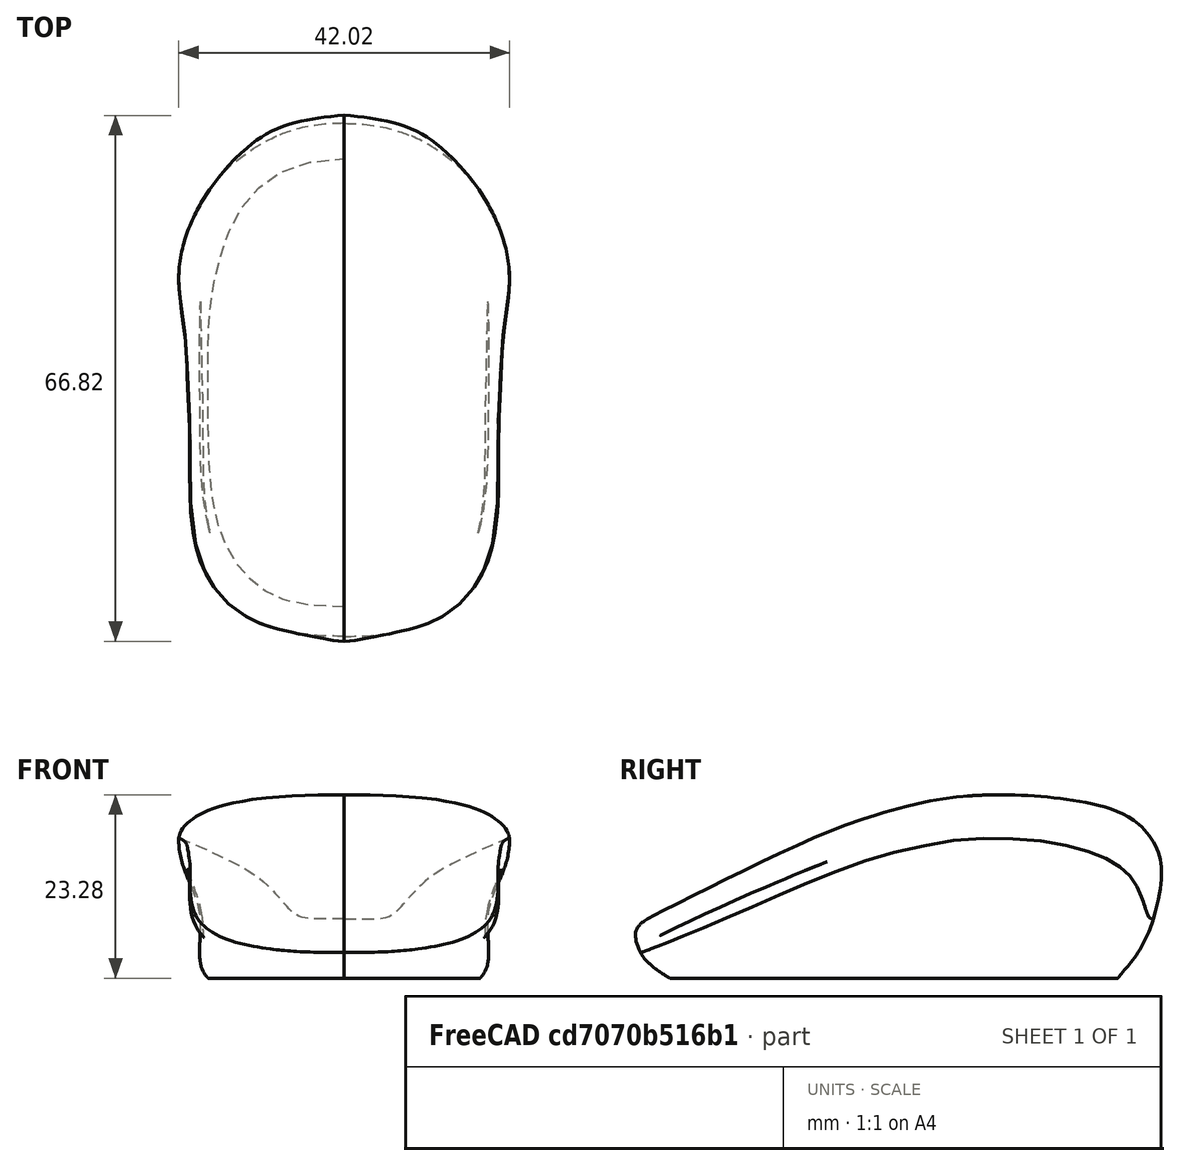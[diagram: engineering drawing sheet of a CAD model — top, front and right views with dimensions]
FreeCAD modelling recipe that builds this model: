
FCSTD DOCUMENT  (FreeCAD 1.0R38643 (Git))
Label: mouse
License: All rights reserved
LicenseURL: http://en.wikipedia.org/wiki/All_rights_reserved
objects: Part::FeaturePython×15, Sketcher::SketchObject×8, Image::ImagePlane×2, Part::Feature×2, Part::Mirroring×1, Part::RuledSurface×1, PartDesign::FeatureBase×1, PartDesign::Body×1, App::DocumentObjectGroup×1
note: 38 computed .brp shape members not serialized (recipe doc carries the construction recipe); baked Part::Feature solids carry a one-line shape summary decoded from their .brp

FEATURE [Image::ImagePlane] ai_mouse_top  label="ai-mouse-top"
  Placement = pos=(0,0,0) rot=(0,0,1;3.14159rad)
  XSize = 43.9769
  YSize = 68
  expr: XSize = 49.28 / 76.2 * YSize
FEATURE [Image::ImagePlane] ai_mouse_side  label="ai-mouse-side"
  Placement = pos=(-2.6e-15,0,11.5) rot=(-0.707107,0,-0.707107;3.14159rad)
  XSize = 31.4299
  YSize = 68
  expr: XSize = 35.22 / 76.2 * YSize
FEATURE [Sketcher::SketchObject] Sketch
  ArcFitTolerance = 0
  FullyConstrained = false
  MakeInternals = false
  sketch-geometry (33):
    g0-g16: Circle [constr] x17 (B-spline internal-alignment scaffolding for g17; pole/knot coordinates omitted)
    g17: BSplineCurve PolesCount=17 KnotsCount=15 Degree=3 IsPeriodic=0
    g18-g32: GeomPoint [constr] x15 (B-spline internal-alignment scaffolding for g17; pole/knot coordinates omitted)
  constraints (9):
    c: Weight(g0) = 1
    c: Equal(g0, g1-g16) x16
    c: InternalAlignment(g0-g16 -> g17) x17
    c: InternalAlignment(g18-g32 -> g17) x15
    c: PointOnObject(g0,g-2)
    c: PointOnObject(g7,g-1)
    c: PointOnObject(g16,g-2)
    c: Horizontal(g1,g17)
    c: Horizontal(g17,g15)
FEATURE [Sketcher::SketchObject] Sketch001
  ArcFitTolerance = 0
  ExternalGeometry = -> [Sketch]
  FullyConstrained = false
  MakeInternals = false
  Placement = pos=(0,0,0) rot=(0.57735,0.57735,0.57735;2.0944rad)
  sketch-geometry (29):
    g0: LineSegment [constr] StartX=-32.3494 StartY=0 StartZ=0 EndX=-32.3494 EndY=16.7331 EndZ=0
    g1: LineSegment [constr] StartX=32.8081 StartY=0 StartZ=0 EndX=32.8081 EndY=17.4154 EndZ=0
    g2-g15: Circle [constr] x14 (B-spline internal-alignment scaffolding for g16; pole/knot coordinates omitted)
    g16: BSplineCurve PolesCount=14 KnotsCount=12 Degree=3 IsPeriodic=0
    g17-g28: GeomPoint [constr] x12 (B-spline internal-alignment scaffolding for g16; pole/knot coordinates omitted)
  constraints (12):
    c: Coincident(g0,g-3)
    c: Vertical(g0)
    c: Coincident(g1,g-3)
    c: Vertical(g1)
    c: Weight(g2) = 1
    c: Equal(g2, g3-g15) x13
    c: InternalAlignment(g2-g15 -> g16) x14
    c: InternalAlignment(g17-g28 -> g16) x12
    c: PointOnObject(g3,g0)
    c: PointOnObject(g27,g1)
    c: Horizontal(g13,g27)
    c: Horizontal(g12,g13)
FEATURE [Part::FeaturePython] Mixed_curve  # WARN: FeaturePython — macro-defined, semantics opaque (R4)
  Active = false
  ApproxTolerance = 0.001
  Continuity = 5
  DegreeMax = 5
  DegreeMin = 3
  Direction1 = (0,0,0)
  Direction2 = (0,0,0)
  FillFace1 = false
  FillFace2 = false
  Parametrization = 0
  Samples = 100
  Shape1 = -> Sketch
  Shape2 = -> Sketch001
FEATURE [Sketcher::SketchObject] Sketch002
  ArcFitTolerance = 0
  ExternalGeometry = -> [Mixed_curve]
  FullyConstrained = false
  MakeInternals = false
  Placement = pos=(0,0,0) rot=(0.57735,0.57735,0.57735;2.0944rad)
  sketch-geometry (45):
    g0-g3: Circle [constr] x4 (B-spline internal-alignment scaffolding for g4; pole/knot coordinates omitted)
    g4: BSplineCurve PolesCount=4 KnotsCount=2 Degree=3 IsPeriodic=0
    g5: GeomPoint [constr] X=-28.6373 Y=0 Z=0
    g6: GeomPoint [constr] X=-32.3494 Y=3.25098 Z=0
    g7-g19: Circle [constr] x13 (B-spline internal-alignment scaffolding for g20; pole/knot coordinates omitted)
    g20: BSplineCurve PolesCount=13 KnotsCount=11 Degree=3 IsPeriodic=0
    g21-g31: GeomPoint [constr] x11 (B-spline internal-alignment scaffolding for g20; pole/knot coordinates omitted)
    g32-g36: Circle [constr] x5 (B-spline internal-alignment scaffolding for g37; pole/knot coordinates omitted)
    g37: BSplineCurve PolesCount=5 KnotsCount=3 Degree=3 IsPeriodic=0
    g38: GeomPoint [constr] X=32.8081 Y=7.53838 Z=0
    g39: GeomPoint [constr] X=30.7658 Y=3.14141 Z=0
    g40: GeomPoint [constr] X=28.2983 Y=0 Z=0
    g41: LineSegment [constr] StartX=-32.3494 StartY=3.25098 StartZ=0 EndX=-33.3149 EndY=5.18964 EndZ=0
    g42: LineSegment [constr] StartX=-32.3494 StartY=3.25098 StartZ=0 EndX=-31.6888 EndY=1.92452 EndZ=0
    g43: LineSegment [constr] StartX=32.8081 StartY=7.53838 StartZ=0 EndX=33.3398 EndY=9.66521 EndZ=0
    g44: LineSegment [constr] StartX=32.8081 StartY=7.53838 StartZ=0 EndX=32.5169 EndY=6.37396 EndZ=0
  constraints (33):
    c: Weight(g0) = 1
    c: Equal(g0,g1)
    c: Equal(g0,g2)
    c: Equal(g0,g3)
    c: InternalAlignment(g0-g3 -> g4) x4
    c: InternalAlignment(g5,g4)
    c: InternalAlignment(g6,g4)
    c: PointOnObject(g0,g-1)
    c: Coincident(g3,g-3)
    c: Weight(g7) = 1
    c: Equal(g7, g8-g19) x12
    c: InternalAlignment(g7-g19 -> g20) x13
    c: InternalAlignment(g21-g31 -> g20) x11
    c: Coincident(g7,g4)
    c: Coincident(g19,g-3)
    c: Weight(g32) = 1
    c: Equal(g32, g33-g36) x4
    c: InternalAlignment(g32-g36 -> g37) x5
    c: InternalAlignment(g38,g37)
    c: InternalAlignment(g39,g37)
    c: InternalAlignment(g40,g37)
    c: Coincident(g32,g20)
    c: PointOnObject(g36,g-1)
    c: Coincident(g41,g20)
    c: Coincident(g41,g8)
    c: Coincident(g42,g3)
    c: Coincident(g42,g2)
    c: Parallel(g41,g42)
    c: Coincident(g43,g37)
    c: Coincident(g43,g18)
    c: Coincident(g44,g19)
    c: Coincident(g44,g33)
    c: Parallel(g43,g44)
FEATURE [Sketcher::SketchObject] Sketch003
  ArcFitTolerance = 0
  ExternalGeometry = -> [Sketch002]
  FullyConstrained = false
  MakeInternals = false
  sketch-geometry (15):
    g0-g7: Circle [constr] x8 (B-spline internal-alignment scaffolding for g8; pole/knot coordinates omitted)
    g8: BSplineCurve PolesCount=8 KnotsCount=6 Degree=3 IsPeriodic=0
    g9-g14: GeomPoint [constr] x6 (B-spline internal-alignment scaffolding for g8; pole/knot coordinates omitted)
  constraints (9):
    c: Weight(g0) = 1
    c: Equal(g0, g1-g7) x7
    c: InternalAlignment(g0-g7 -> g8) x8
    c: InternalAlignment(g9-g14 -> g8) x6
    c: Coincident(g0,g-3)
    c: PointOnObject(g3,g-1)
    c: Coincident(g7,g-4)
    c: Horizontal(g8,g1)
    c: Horizontal(g8,g6)
FEATURE [Part::FeaturePython] Freehand_BSpline  # WARN: FeaturePython — macro-defined, semantics opaque (R4)
  Data = (5) [(20.9782,12.1976,17.7693),(20.7313,12.1868,15.241),(18.3975,12.1913,8.67744),(17.7344,12.1956,2.33636),(16.5708,12.2001,0)]
  DataType = [1,0,0,0,1]
  Parametrization = 1
  Periodic = false
  Support = -> [Mixed_curve,Sketch003]
  Tangents = (5) [(0,0,0),(0,0,0),(0,0,0),(0,0,0),(0,0,0)]
  Tolerance = 1e-07
FEATURE [Part::FeaturePython] JoinCurve  # WARN: FeaturePython — macro-defined, semantics opaque (R4)
  Active = false
  ApproxTolerance = 0.001
  Continuity = 5
  CornerBreak = false
  DegreeMax = 5
  DegreeMin = 3
  Edges = -> [Sketch002]
  ForceClosed = false
  ForceContact = true
  Parametrization = 0
  Reverse = false
  Samples = 100
  StartOffset = 0
  Tolerance = 0.01
FEATURE [Part::FeaturePython] JoinCurve001  # WARN: FeaturePython — macro-defined, semantics opaque (R4)
  Active = false
  ApproxTolerance = 0.001
  Continuity = 5
  CornerBreak = false
  DegreeMax = 5
  DegreeMin = 3
  Edges = -> [Sketch002]
  ForceClosed = false
  ForceContact = true
  Parametrization = 0
  Reverse = false
  Samples = 100
  StartOffset = 0
  Tolerance = 0.01
FEATURE [Part::FeaturePython] JoinCurve002  # WARN: FeaturePython — macro-defined, semantics opaque (R4)
  Active = false
  ApproxTolerance = 0.001
  Continuity = 5
  CornerBreak = false
  DegreeMax = 5
  DegreeMin = 3
  Edges = -> [Sketch003]
  ForceClosed = false
  ForceContact = true
  Parametrization = 0
  Reverse = false
  Samples = 100
  StartOffset = 0
  Tolerance = 0.01
FEATURE [Part::FeaturePython] Gordon  # WARN: FeaturePython — macro-defined, semantics opaque (R4)
  FlipNormal = false
  MaxCtrlPts = 80
  Output = 0
  SamplesU = 16
  SamplesV = 16
  Sources = -> [Mixed_curve,JoinCurve002,JoinCurve,Freehand_BSpline,JoinCurve001]
  Tol2D = 1e-05
  Tol3D = 0.01
FEATURE [Part::FeaturePython] Freehand_BSpline001  # WARN: FeaturePython — macro-defined, semantics opaque (R4)
  Data = (2) [(13.658,-28.9898,4.51691),(0,-31.4534,7.51518)]
  DataType = [1,1]
  Parametrization = 1
  Periodic = false
  Support = -> [Mixed_curve,Sketch002]
  Tangents = (2) [(0,0,0),(0,0,0)]
  Tolerance = 1e-07
FEATURE [Part::FeaturePython] Freehand_BSpline002  # WARN: FeaturePython — macro-defined, semantics opaque (R4)
  Data = (2) [(21.0023,12.8859,17.7665),(0,12.7657,23.283)]
  DataType = [1,1]
  Parametrization = 1
  Periodic = false
  Support = -> [Mixed_curve,Sketch002]
  Tangents = (2) [(0,0,0),(0,0,0)]
  Tolerance = 1e-07
FEATURE [Part::FeaturePython] Freehand_BSpline003  # WARN: FeaturePython — macro-defined, semantics opaque (R4)
  Data = (2) [(13.7278,28.0021,14.4972),(0,30.9529,19.5086)]
  DataType = [1,1]
  Parametrization = 1
  Periodic = false
  Support = -> [Mixed_curve,Sketch002]
  Tangents = (2) [(0,0,0),(0,0,0)]
  Tolerance = 1e-07
FEATURE [Sketcher::SketchObject] Sketch004
  ArcFitTolerance = 0
  ExternalGeometry = -> [Freehand_BSpline001,Freehand_BSpline002,Freehand_BSpline003]
  FullyConstrained = true
  MakeInternals = false
  Placement = pos=(0,0,0) rot=(0.57735,0.57735,0.57735;2.0944rad)
  sketch-geometry (3):
    g0: LineSegment StartX=-31.4534 StartY=7.51518 StartZ=0 EndX=-28.9898 EndY=4.51691 EndZ=0
    g1: LineSegment StartX=12.7657 StartY=23.283 StartZ=0 EndX=12.8859 EndY=17.7665 EndZ=0
    g2: LineSegment StartX=30.9529 StartY=19.5086 StartZ=0 EndX=28.0021 EndY=14.4972 EndZ=0
  constraints (6):
    c: Coincident(g0,g-3)
    c: Coincident(g0,g-3)
    c: Coincident(g1,g-4)
    c: Coincident(g1,g-4)
    c: Coincident(g2,g-5)
    c: Coincident(g2,g-5)
FEATURE [Sketcher::SketchObject] Sketch005
  ArcFitTolerance = 0
  ExternalGeometry = -> [Freehand_BSpline001]
  FullyConstrained = false
  MakeInternals = false
  MapMode = 13
  Placement = pos=(4.55267,-29.811,5.51633) rot=(1,0,0;2.25861rad)
  sketch-geometry (17):
    g0-g8: Circle [constr] x9 (B-spline internal-alignment scaffolding for g9; pole/knot coordinates omitted)
    g9: BSplineCurve PolesCount=9 KnotsCount=7 Degree=3 IsPeriodic=0
    g10-g16: GeomPoint [constr] x7 (B-spline internal-alignment scaffolding for g9; pole/knot coordinates omitted)
  constraints (7):
    c: Weight(g0) = 1
    c: Equal(g0, g1-g8) x8
    c: InternalAlignment(g0-g8 -> g9) x9
    c: InternalAlignment(g10-g16 -> g9) x7
    c: Coincident(g0,g-3)
    c: Coincident(g8,g-3)
    c: Horizontal(g9,g1)
FEATURE [Sketcher::SketchObject] Sketch006
  ArcFitTolerance = 0
  ExternalGeometry = -> [Freehand_BSpline002]
  FullyConstrained = false
  MakeInternals = false
  MapMode = 13
  Placement = pos=(7.00076,12.8459,19.6053) rot=(0,0.699363,0.714767;3.14159rad)
  sketch-geometry (11):
    g0-g5: Circle [constr] x6 (B-spline internal-alignment scaffolding for g6; pole/knot coordinates omitted)
    g6: BSplineCurve PolesCount=6 KnotsCount=4 Degree=3 IsPeriodic=0
    g7-g10: GeomPoint [constr] x4 (B-spline internal-alignment scaffolding for g6; pole/knot coordinates omitted)
  constraints (7):
    c: Weight(g0) = 1
    c: Equal(g0, g1-g5) x5
    c: InternalAlignment(g0-g5 -> g6) x6
    c: InternalAlignment(g7-g10 -> g6) x4
    c: Coincident(g0,g-3)
    c: Coincident(g5,g-3)
    c: Horizontal(g6,g1)
FEATURE [Sketcher::SketchObject] Sketch007
  ArcFitTolerance = 0
  ExternalGeometry = -> [Freehand_BSpline003]
  FullyConstrained = false
  MakeInternals = false
  MapMode = 13
  Placement = pos=(4.57594,28.9857,16.1677) rot=(0,0.868155,0.496293;3.14159rad)
  sketch-geometry (11):
    g0-g5: Circle [constr] x6 (B-spline internal-alignment scaffolding for g6; pole/knot coordinates omitted)
    g6: BSplineCurve PolesCount=6 KnotsCount=4 Degree=3 IsPeriodic=0
    g7-g10: GeomPoint [constr] x4 (B-spline internal-alignment scaffolding for g6; pole/knot coordinates omitted)
  constraints (7):
    c: Weight(g0) = 1
    c: Equal(g0, g1-g5) x5
    c: InternalAlignment(g0-g5 -> g6) x6
    c: InternalAlignment(g7-g10 -> g6) x4
    c: Coincident(g0,g-3)
    c: Coincident(g5,g-3)
    c: Horizontal(g1,g6)
FEATURE [Part::FeaturePython] SplitCurve  # WARN: FeaturePython — macro-defined, semantics opaque (R4)
  CutAtVertexes = false
  Distance = 0
  KeepSolid = false
  NormalizedParameters = [0,0.0899253,0.18748,0.285034,0.382588,0.484761,0.58781,0.690859,0.793904,0.896953,1]
  Number = 10
  Source = -> Mixed_curve [Edge1]
FEATURE [Part::FeaturePython] JoinCurve003  # WARN: FeaturePython — macro-defined, semantics opaque (R4)
  Active = false
  ApproxTolerance = 0.001
  Continuity = 5
  CornerBreak = false
  DegreeMax = 5
  DegreeMin = 3
  Edges = -> [SplitCurve]
  ForceClosed = false
  ForceContact = true
  Parametrization = 0
  Reverse = false
  Samples = 100
  StartOffset = 0
  Tolerance = 0.01
FEATURE [Part::FeaturePython] JoinCurve004  # WARN: FeaturePython — macro-defined, semantics opaque (R4)
  Active = false
  ApproxTolerance = 0.001
  Continuity = 5
  CornerBreak = false
  DegreeMax = 5
  DegreeMin = 3
  Edges = -> [SplitCurve]
  ForceClosed = false
  ForceContact = true
  Parametrization = 0
  Reverse = false
  Samples = 100
  StartOffset = 0
  Tolerance = 0.01
FEATURE [Part::FeaturePython] JoinCurve005  # WARN: FeaturePython — macro-defined, semantics opaque (R4)
  Active = false
  ApproxTolerance = 0.001
  Continuity = 5
  CornerBreak = false
  DegreeMax = 5
  DegreeMin = 3
  Edges = -> [SplitCurve]
  ForceClosed = false
  ForceContact = true
  Parametrization = 0
  Reverse = false
  Samples = 100
  StartOffset = 0
  Tolerance = 0.01
FEATURE [Part::FeaturePython] Gordon001  # WARN: FeaturePython — macro-defined, semantics opaque (R4)
  FlipNormal = false
  MaxCtrlPts = 80
  Output = 0
  SamplesU = 16
  SamplesV = 16
  Sources = -> [Sketch002,JoinCurve003,JoinCurve004,Sketch005,Sketch006,Sketch007,JoinCurve005]
  Tol2D = 1e-05
  Tol3D = 0.01
FEATURE [Part::FeaturePython] Connect  # WARN: FeaturePython — macro-defined, semantics opaque (R4)
  Objects = -> [Gordon001,Gordon]
  Tolerance = 0.01
FEATURE [Part::Mirroring] Part__Mirroring  label="Connect (Mirror #1)"
  Base = (0,0,0)
  Normal = (1,0,0)
  Source = -> Connect
FEATURE [Part::RuledSurface] Ruled_Surface
  Curve1 = -> Part__Mirroring [Edge5]
  Curve2 = -> Connect [Edge5]
  Orientation = 0
FEATURE [Part::Feature] Shell
  shape: bbox 42.06 x 66.89 x 23.29 mm, 5 faces, 0 solids (baked)
FEATURE [Part::Feature] Solid
  shape: bbox 42.06 x 66.89 x 23.29 mm, 5 faces (baked)
FEATURE [PartDesign::FeatureBase] BaseFeature
  BaseFeature = -> Solid
  Suppressed = false
FEATURE [PartDesign::Body] Body
  AllowCompound = false
  BaseFeature = -> Solid
  Group = -> [BaseFeature]
  Origin = -> Origin
  Tip = -> BaseFeature
FEATURE [App::DocumentObjectGroup] Group  label="mouse_solid"
  Group = -> [ai_mouse_side,ai_mouse_top,Freehand_BSpline003,Sketch003,Solid,Freehand_BSpline001,Freehand_BSpline002,Sketch004,SplitCurve,Ruled_Surface,Shell]
